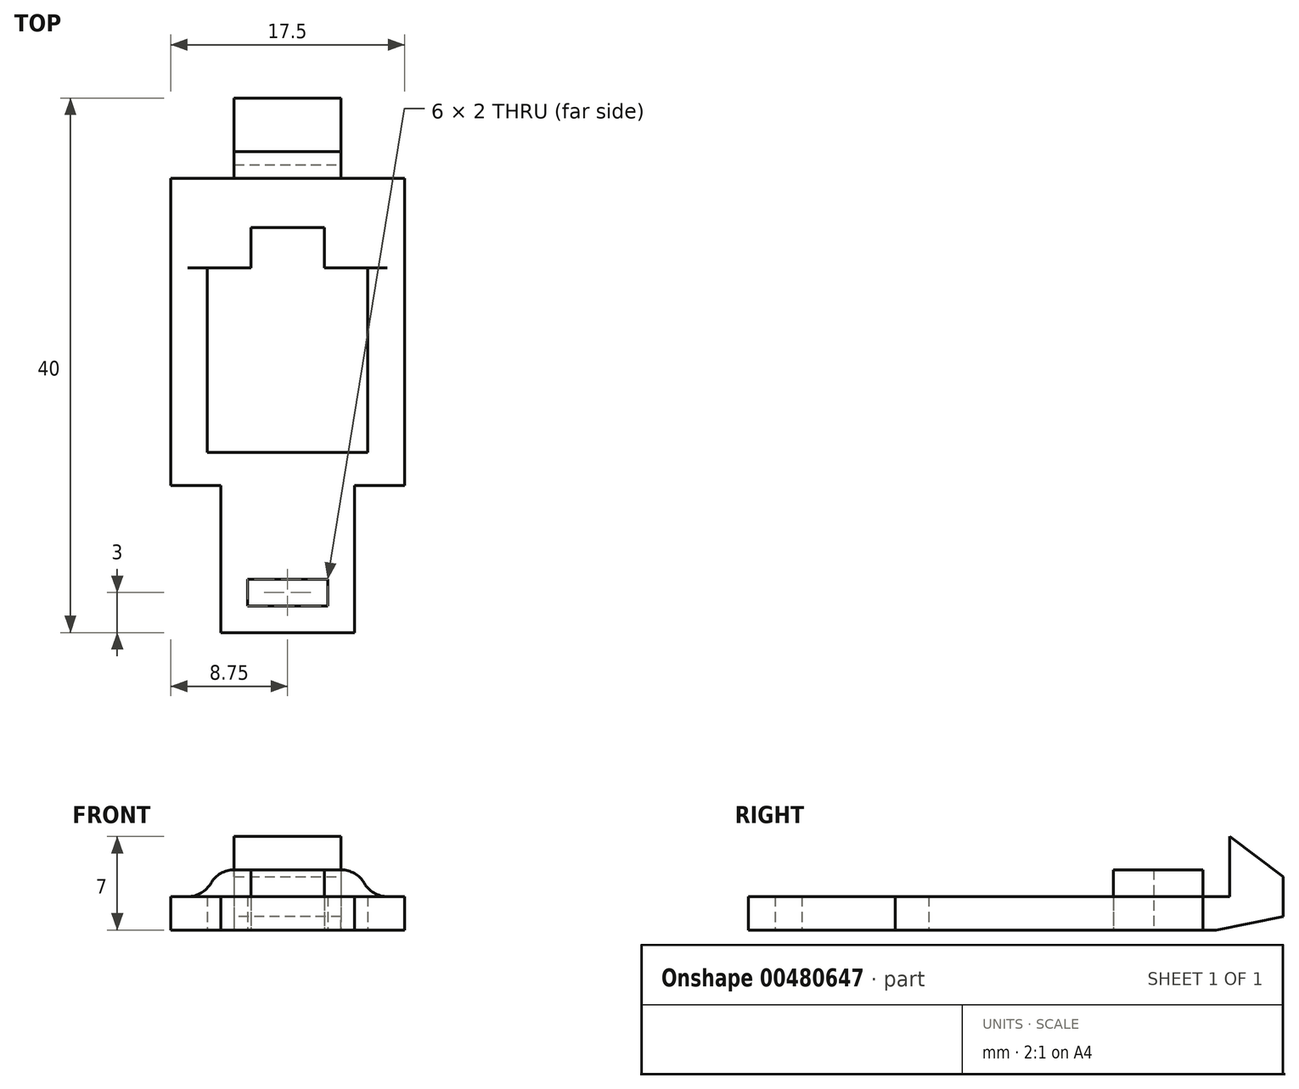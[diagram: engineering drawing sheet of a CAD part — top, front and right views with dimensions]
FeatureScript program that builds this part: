
annotation { "Feature Type Name" : "Feature", "Feature Type Description" : "" }
export const myFeature = defineFeature(function(context is Context, id is Id, definition is map)
    precondition{}
    {
        {
            var Q0;
            Q0=qCreatedBy(makeId("Top.planeOp"),FACE);
            var sketch = newSketch(context, id + "F0", { "sketchPlane" : qUnion([Q0])});
            skLineSegment(sketch, "E0.top", {"start": v(-5, 0) * mm, "end": v(5, 0) * mm});
            skLineSegment(sketch, "E0.left", {"start": v(-5, 11) * mm, "end": v(-5, 0) * mm});
            skLineSegment(sketch, "E0.right", {"start": v(5, 11) * mm, "end": v(5, 0) * mm});
            skLineSegment(sketch, "E1.bottom", {"start": v(-3, 4) * mm, "end": v(3, 4) * mm});
            skLineSegment(sketch, "E1.top", {"start": v(-3, 2) * mm, "end": v(3, 2) * mm});
            skLineSegment(sketch, "E1.left", {"start": v(-3, 4) * mm, "end": v(-3, 2) * mm});
            skLineSegment(sketch, "E1.right", {"start": v(3, 4) * mm, "end": v(3, 2) * mm});
            skLineSegment(sketch, "E2.left", {"start": v(-8.75, 34) * mm, "end": v(-8.75, 11) * mm});
            skLineSegment(sketch, "E3.bottom", {"start": v(-6, 27.31) * mm, "end": v(-2.75, 27.31) * mm});
            skLineSegment(sketch, "E3.top", {"start": v(-6, 13.5) * mm, "end": v(6, 13.5) * mm});
            skLineSegment(sketch, "E4.trimOffspring", {"start": v(2.75, 27.31) * mm, "end": v(6, 27.31) * mm});
            skLineSegment(sketch, "E5.bottom", {"start": v(-4, 40) * mm, "end": v(4, 40) * mm});
            skLineSegment(sketch, "E5.left", {"start": v(-4, 40) * mm, "end": v(-4, 34) * mm});
            skLineSegment(sketch, "E6", {"start": v(-8.75, 11) * mm, "end": v(-5, 11) * mm});
            skLineSegment(sketch, "E7.trimOffspring", {"start": v(5, 11) * mm, "end": v(8.75, 11) * mm});
            skLineSegment(sketch, "E8", {"start": v(-8.75, 34) * mm, "end": v(-4, 34) * mm});
            skLineSegment(sketch, "E9.MirrorCS", {"start": v(4, 40) * mm, "end": v(4, 34) * mm});
            skLineSegment(sketch, "E10.MirrorCS", {"start": v(8.75, 34) * mm, "end": v(8.75, 11) * mm});
            skLineSegment(sketch, "E11.1.0.0", {"start": v(-6, 27.31) * mm, "end": v(-6, 13.5) * mm});
            skLineSegment(sketch, "E12.MirrorCS", {"start": v(6, 27.31) * mm, "end": v(6, 13.5) * mm});
            skLineSegment(sketch, "E13.trimOffspring", {"start": v(8.75, 34) * mm, "end": v(4, 34) * mm});
            skLineSegment(sketch, "E14.left", {"start": v(-2.75, 30.31) * mm, "end": v(-2.75, 27.31) * mm});
            skLineSegment(sketch, "E14.right", {"start": v(2.75, 30.31) * mm, "end": v(2.75, 27.31) * mm});
            skLineSegment(sketch, "E15", {"start": v(-2.75, 30.31) * mm, "end": v(2.75, 30.31) * mm});
            skSolve(sketch);
        }
        {
            var Q0;
            Q0 = qSketchRegion(id + "F0", true);
            extrude(context, id + "F1", {"entities" : qUnion([Q0]), "depth" : 2.5 * mm});
        }
        {
            var Q0;
            Q0=makeQuery(id+"F1.opExtrude","CAP_FACE",FACE,{"disambiguationData":[OSD([sQuery(id+"F0.wireOp",EDGE,"c61d65e6-1c6f-470b-8ea6-7b39f012f9b7.left"),sQuery(id+"F0.wireOp",EDGE,"70c6a211-a52c-406c-92e0-63f975188017.bottom"),sQuery(id+"F0.wireOp",EDGE,"70c6a211-a52c-406c-92e0-63f975188017.top"),sQuery(id+"F0.wireOp",EDGE,"65aeff96-546b-4572-a45a-624273845dfc.top"),sQuery(id+"F0.wireOp",EDGE,"65aeff96-546b-4572-a45a-624273845dfc.left"),sQuery(id+"F0.wireOp",EDGE,"65aeff96-546b-4572-a45a-624273845dfc.right"),sQuery(id+"F0.wireOp",EDGE,"a518adc7-5a1b-4d6e-859b-b4c8afc186f1.trimOffspring"),sQuery(id+"F0.wireOp",EDGE,"6987841f-cc05-4c10-9104-1d9a40be5a12.bottom"),sQuery(id+"F0.wireOp",EDGE,"6987841f-cc05-4c10-9104-1d9a40be5a12.left"),sQuery(id+"F0.wireOp",EDGE,"E0.top"),sQuery(id+"F0.wireOp",EDGE,"E0.left"),sQuery(id+"F0.wireOp",EDGE,"E0.right"),sQuery(id+"F0.wireOp",EDGE,"E1.bottom"),sQuery(id+"F0.wireOp",EDGE,"E1.top"),sQuery(id+"F0.wireOp",EDGE,"E1.left"),sQuery(id+"F0.wireOp",EDGE,"E1.right"),sQuery(id+"F0.wireOp",EDGE,"f09f0b5b-2907-45f8-9cf5-e8af5dd8afe1"),sQuery(id+"F0.wireOp",EDGE,"02a836fe-445c-472a-9bd4-455a8fe9fec3.trimOffspring"),sQuery(id+"F0.wireOp",EDGE,"f463603e-5eee-4f32-b9c0-3652a566a423"),sQuery(id+"F0.wireOp",EDGE,"7cbc7dd2-0c68-4058-8ebc-1e7dea4ef9cb.MirrorCS"),sQuery(id+"F0.wireOp",EDGE,"0120faa1-c2c2-48c8-9fb2-8a26d659d6d3.MirrorCS"),sQuery(id+"F0.wireOp",EDGE,"2528b15f-6ecc-4ec7-a502-4d260d87d49d.1.0.0"),sQuery(id+"F0.wireOp",EDGE,"fe2906e0-b90a-4319-b7dc-69472c8c5e2e.MirrorCS"),sQuery(id+"F0.wireOp",EDGE,"78b9e663-7a5b-452b-955c-902cd374385f.trimOffspring")])],"isStart":false});
            var sketch = newSketch(context, id + "F2", { "sketchPlane" : qUnion([Q0])});
            skLineSegment(sketch, "E16.bottom", {"start": v(-4, 40) * mm, "end": v(4, 40) * mm});
            skLineSegment(sketch, "E16.top", {"start": v(-4, 36) * mm, "end": v(4, 36) * mm});
            skLineSegment(sketch, "E16.left", {"start": v(-4, 40) * mm, "end": v(-4, 36) * mm});
            skLineSegment(sketch, "E16.right", {"start": v(4, 40) * mm, "end": v(4, 36) * mm});
            skSolve(sketch);
        }
        {
            var Q0;
            Q0 = qSketchRegion(id + "F2", true);
            extrude(context, id + "F3", {"entities" : qUnion([Q0]), "operationType" : NewBodyOperationType.ADD, "depth" : 4.5 * mm});
        }
        {
            var Q0;
            Q0=makeQuery(id+"F3.opExtrude","CAP_EDGE",EDGE,{"disambiguationData":[OSD([sQuery(id+"F2.wireOp",EDGE,"E16.bottom")])],"isStart":false});
            chamfer(context, id + "F4", {"entities" : qUnion([Q0]), "chamferType" : ChamferType.TWO_OFFSETS, "width1" : 3 * mm, "oppositeDirection" : false, "width2" : 4 * mm, "tangentPropagation" : true});
        }
        {
            var Q0;
            Q0=makeQuery(id+"F1.opExtrude","CAP_EDGE",EDGE,{"disambiguationData":[OSD([sQuery(id+"F0.wireOp",EDGE,"E5.bottom")])],"isStart":true});
            chamfer(context, id + "F5", {"entities" : qUnion([Q0]), "chamferType" : ChamferType.TWO_OFFSETS, "width1" : 5 * mm, "oppositeDirection" : false, "width2" : 1 * mm, "tangentPropagation" : true});
        }
        {
            var Q0;
            Q0=makeQuery(id+"F1.opExtrude","CAP_FACE",FACE,{"disambiguationData":[OSD([sQuery(id+"F0.wireOp",EDGE,"E0.top"),sQuery(id+"F0.wireOp",EDGE,"E0.left"),sQuery(id+"F0.wireOp",EDGE,"E0.right"),sQuery(id+"F0.wireOp",EDGE,"E1.bottom"),sQuery(id+"F0.wireOp",EDGE,"E1.top"),sQuery(id+"F0.wireOp",EDGE,"E1.left"),sQuery(id+"F0.wireOp",EDGE,"E1.right"),sQuery(id+"F0.wireOp",EDGE,"E2.left"),sQuery(id+"F0.wireOp",EDGE,"E3.bottom"),sQuery(id+"F0.wireOp",EDGE,"E3.top"),sQuery(id+"F0.wireOp",EDGE,"E4.trimOffspring"),sQuery(id+"F0.wireOp",EDGE,"E5.bottom"),sQuery(id+"F0.wireOp",EDGE,"E5.left"),sQuery(id+"F0.wireOp",EDGE,"E6"),sQuery(id+"F0.wireOp",EDGE,"E7.trimOffspring"),sQuery(id+"F0.wireOp",EDGE,"E8"),sQuery(id+"F0.wireOp",EDGE,"E9.MirrorCS"),sQuery(id+"F0.wireOp",EDGE,"E10.MirrorCS"),sQuery(id+"F0.wireOp",EDGE,"E11.1.0.0"),sQuery(id+"F0.wireOp",EDGE,"E12.MirrorCS"),sQuery(id+"F0.wireOp",EDGE,"E13.trimOffspring"),sQuery(id+"F0.wireOp",EDGE,"E14.left"),sQuery(id+"F0.wireOp",EDGE,"E14.right"),sQuery(id+"F0.wireOp",EDGE,"E15")])],"isStart":false});
            var sketch = newSketch(context, id + "F6", { "sketchPlane" : qUnion([Q0])});
            skLineSegment(sketch, "E17.bottom", {"start": v(6, 27.31) * mm, "end": v(2.75, 27.31) * mm});
            skLineSegment(sketch, "E17.top", {"start": v(6, 34) * mm, "end": v(-6, 34) * mm});
            skLineSegment(sketch, "E17.left", {"start": v(6, 27.31) * mm, "end": v(6, 34) * mm});
            skLineSegment(sketch, "E17.right", {"start": v(-6, 27.31) * mm, "end": v(-6, 34) * mm});
            skLineSegment(sketch, "E18", {"start": v(-2.75, 27.31) * mm, "end": v(-2.75, 30.31) * mm});
            skLineSegment(sketch, "E19", {"start": v(-2.75, 30.31) * mm, "end": v(2.75, 30.31) * mm});
            skLineSegment(sketch, "E20", {"start": v(2.75, 30.31) * mm, "end": v(2.75, 27.31) * mm});
            skLineSegment(sketch, "E21.trimOffspring", {"start": v(-2.75, 27.31) * mm, "end": v(-6, 27.31) * mm});
            skSolve(sketch);
        }
        {
            var Q0;
            Q0 = qSketchRegion(id + "F6", true);
            extrude(context, id + "F7", {"entities" : qUnion([Q0]), "operationType" : NewBodyOperationType.ADD, "depth" : 2 * mm, "offsetDistance" : 25 * mm});
        }
        {
            var Q0;
            Q0=makeQuery(id+"F7.opExtrude","CAP_EDGE",EDGE,{"disambiguationData":[OSD([sQuery(id+"F6.wireOp",EDGE,"E17.right")])],"isStart":false});
            var Q1;
            Q1=makeQuery(id+"F7.opExtrude","CAP_EDGE",EDGE,{"disambiguationData":[OSD([sQuery(id+"F6.wireOp",EDGE,"E17.left")])],"isStart":false});
            fillet(context, id + "F8", {"entities" : qUnion([Q0, Q1]), "radius" : 2 * mm, "tangentPropagation" : true, "allowEdgeOverflow" : false});
        }
        {
            var Q0;
            {var subQ0=sQuery(id+"F0.wireOp",EDGE,"E13.trimOffspring");var subQ1=sQuery(id+"F0.wireOp",EDGE,"E12.MirrorCS");var subQ2=sQuery(id+"F0.wireOp",EDGE,"E11.1.0.0");var subQ3=sQuery(id+"F0.wireOp",EDGE,"E10.MirrorCS");var subQ4=sQuery(id+"F0.wireOp",EDGE,"E8");var subQ5=sQuery(id+"F6.wireOp",EDGE,"E17.left");var subQ6=sQuery(id+"F0.wireOp",EDGE,"E7.trimOffspring");var subQ7=sQuery(id+"F0.wireOp",EDGE,"E6");var subQ8=sQuery(id+"F0.wireOp",EDGE,"E4.trimOffspring");var subQ9=sQuery(id+"F0.wireOp",EDGE,"E0.right");var subQ10=sQuery(id+"F0.wireOp",EDGE,"E0.left");var subQ11=sQuery(id+"F0.wireOp",EDGE,"E1.bottom");var subQ12=sQuery(id+"F0.wireOp",EDGE,"E0.top");var subQ13=sQuery(id+"F0.wireOp",EDGE,"E3.top");var subQ14=sQuery(id+"F0.wireOp",EDGE,"E1.top");var subQ15=sQuery(id+"F0.wireOp",EDGE,"E1.left");var subQ16=sQuery(id+"F0.wireOp",EDGE,"E1.right");var subQ17=sQuery(id+"F0.wireOp",EDGE,"E2.left");var subQ18=sQuery(id+"F0.wireOp",EDGE,"E3.bottom");Q0=makeQuery(id+"F8.opFillet","BLEND_EDGE",EDGE,{"blendedFrom":[makeQuery(id+"F7.opExtrude","CAP_EDGE",EDGE,{"disambiguationData":[OSD([subQ5])],"isStart":false}),makeQuery(id+"F7.boolean.opBoolean","SPLIT",FACE,{"disambiguationData":[TD([makeQuery(id+"F1.opExtrude","SWEPT_FACE",FACE,{"disambiguationData":[OSD([subQ12])]})])],"derivedFrom":makeQuery(id+"F1.opExtrude","CAP_FACE",FACE,{"disambiguationData":[OSD([subQ12,subQ10,subQ9,subQ11,subQ14,subQ15,subQ16,subQ17,subQ18,subQ13,subQ8,sQuery(id+"F0.wireOp",EDGE,"E5.bottom"),sQuery(id+"F0.wireOp",EDGE,"E5.left"),subQ7,subQ6,subQ4,sQuery(id+"F0.wireOp",EDGE,"E9.MirrorCS"),subQ3,subQ2,subQ1,subQ0,sQuery(id+"F0.wireOp",EDGE,"E14.left"),sQuery(id+"F0.wireOp",EDGE,"E14.right"),sQuery(id+"F0.wireOp",EDGE,"E15")])],"isStart":false})})],"blendedInto":[makeQuery(id+"F7.boolean.opBoolean","SPLIT",FACE,{"disambiguationData":[TD([makeQuery(id+"F1.opExtrude","SWEPT_FACE",FACE,{"disambiguationData":[OSD([subQ12])]})])],"derivedFrom":makeQuery(id+"F1.opExtrude","CAP_FACE",FACE,{"disambiguationData":[OSD([subQ12,subQ10,subQ9,subQ11,subQ14,subQ15,subQ16,subQ17,subQ18,subQ13,subQ8,sQuery(id+"F0.wireOp",EDGE,"E5.bottom"),sQuery(id+"F0.wireOp",EDGE,"E5.left"),subQ7,subQ6,subQ4,sQuery(id+"F0.wireOp",EDGE,"E9.MirrorCS"),subQ3,subQ2,subQ1,subQ0,sQuery(id+"F0.wireOp",EDGE,"E14.left"),sQuery(id+"F0.wireOp",EDGE,"E14.right"),sQuery(id+"F0.wireOp",EDGE,"E15")])],"isStart":false})})]});}
            var Q1;
            {var subQ0=sQuery(id+"F0.wireOp",EDGE,"E13.trimOffspring");var subQ1=sQuery(id+"F0.wireOp",EDGE,"E12.MirrorCS");var subQ2=sQuery(id+"F0.wireOp",EDGE,"E11.1.0.0");var subQ3=sQuery(id+"F0.wireOp",EDGE,"E10.MirrorCS");var subQ4=sQuery(id+"F6.wireOp",EDGE,"E17.right");var subQ5=sQuery(id+"F0.wireOp",EDGE,"E8");var subQ6=sQuery(id+"F0.wireOp",EDGE,"E7.trimOffspring");var subQ7=sQuery(id+"F0.wireOp",EDGE,"E6");var subQ8=sQuery(id+"F0.wireOp",EDGE,"E4.trimOffspring");var subQ9=sQuery(id+"F0.wireOp",EDGE,"E0.right");var subQ10=sQuery(id+"F0.wireOp",EDGE,"E0.left");var subQ11=sQuery(id+"F0.wireOp",EDGE,"E1.bottom");var subQ12=sQuery(id+"F0.wireOp",EDGE,"E0.top");var subQ13=sQuery(id+"F0.wireOp",EDGE,"E3.top");var subQ14=sQuery(id+"F0.wireOp",EDGE,"E1.top");var subQ15=sQuery(id+"F0.wireOp",EDGE,"E1.left");var subQ16=sQuery(id+"F0.wireOp",EDGE,"E1.right");var subQ17=sQuery(id+"F0.wireOp",EDGE,"E2.left");var subQ18=sQuery(id+"F0.wireOp",EDGE,"E3.bottom");Q1=makeQuery(id+"F8.opFillet","BLEND_EDGE",EDGE,{"blendedFrom":[makeQuery(id+"F7.opExtrude","CAP_EDGE",EDGE,{"disambiguationData":[OSD([subQ4])],"isStart":false}),makeQuery(id+"F7.boolean.opBoolean","SPLIT",FACE,{"disambiguationData":[TD([makeQuery(id+"F1.opExtrude","SWEPT_FACE",FACE,{"disambiguationData":[OSD([subQ12])]})])],"derivedFrom":makeQuery(id+"F1.opExtrude","CAP_FACE",FACE,{"disambiguationData":[OSD([subQ12,subQ10,subQ9,subQ11,subQ14,subQ15,subQ16,subQ17,subQ18,subQ13,subQ8,sQuery(id+"F0.wireOp",EDGE,"E5.bottom"),sQuery(id+"F0.wireOp",EDGE,"E5.left"),subQ7,subQ6,subQ5,sQuery(id+"F0.wireOp",EDGE,"E9.MirrorCS"),subQ3,subQ2,subQ1,subQ0,sQuery(id+"F0.wireOp",EDGE,"E14.left"),sQuery(id+"F0.wireOp",EDGE,"E14.right"),sQuery(id+"F0.wireOp",EDGE,"E15")])],"isStart":false})})],"blendedInto":[makeQuery(id+"F7.boolean.opBoolean","SPLIT",FACE,{"disambiguationData":[TD([makeQuery(id+"F1.opExtrude","SWEPT_FACE",FACE,{"disambiguationData":[OSD([subQ12])]})])],"derivedFrom":makeQuery(id+"F1.opExtrude","CAP_FACE",FACE,{"disambiguationData":[OSD([subQ12,subQ10,subQ9,subQ11,subQ14,subQ15,subQ16,subQ17,subQ18,subQ13,subQ8,sQuery(id+"F0.wireOp",EDGE,"E5.bottom"),sQuery(id+"F0.wireOp",EDGE,"E5.left"),subQ7,subQ6,subQ5,sQuery(id+"F0.wireOp",EDGE,"E9.MirrorCS"),subQ3,subQ2,subQ1,subQ0,sQuery(id+"F0.wireOp",EDGE,"E14.left"),sQuery(id+"F0.wireOp",EDGE,"E14.right"),sQuery(id+"F0.wireOp",EDGE,"E15")])],"isStart":false})})]});}
            fillet(context, id + "F9", {"entities" : qUnion([Q0, Q1]), "radius" : 2 * mm, "tangentPropagation" : true, "allowEdgeOverflow" : false});
        }
    });
